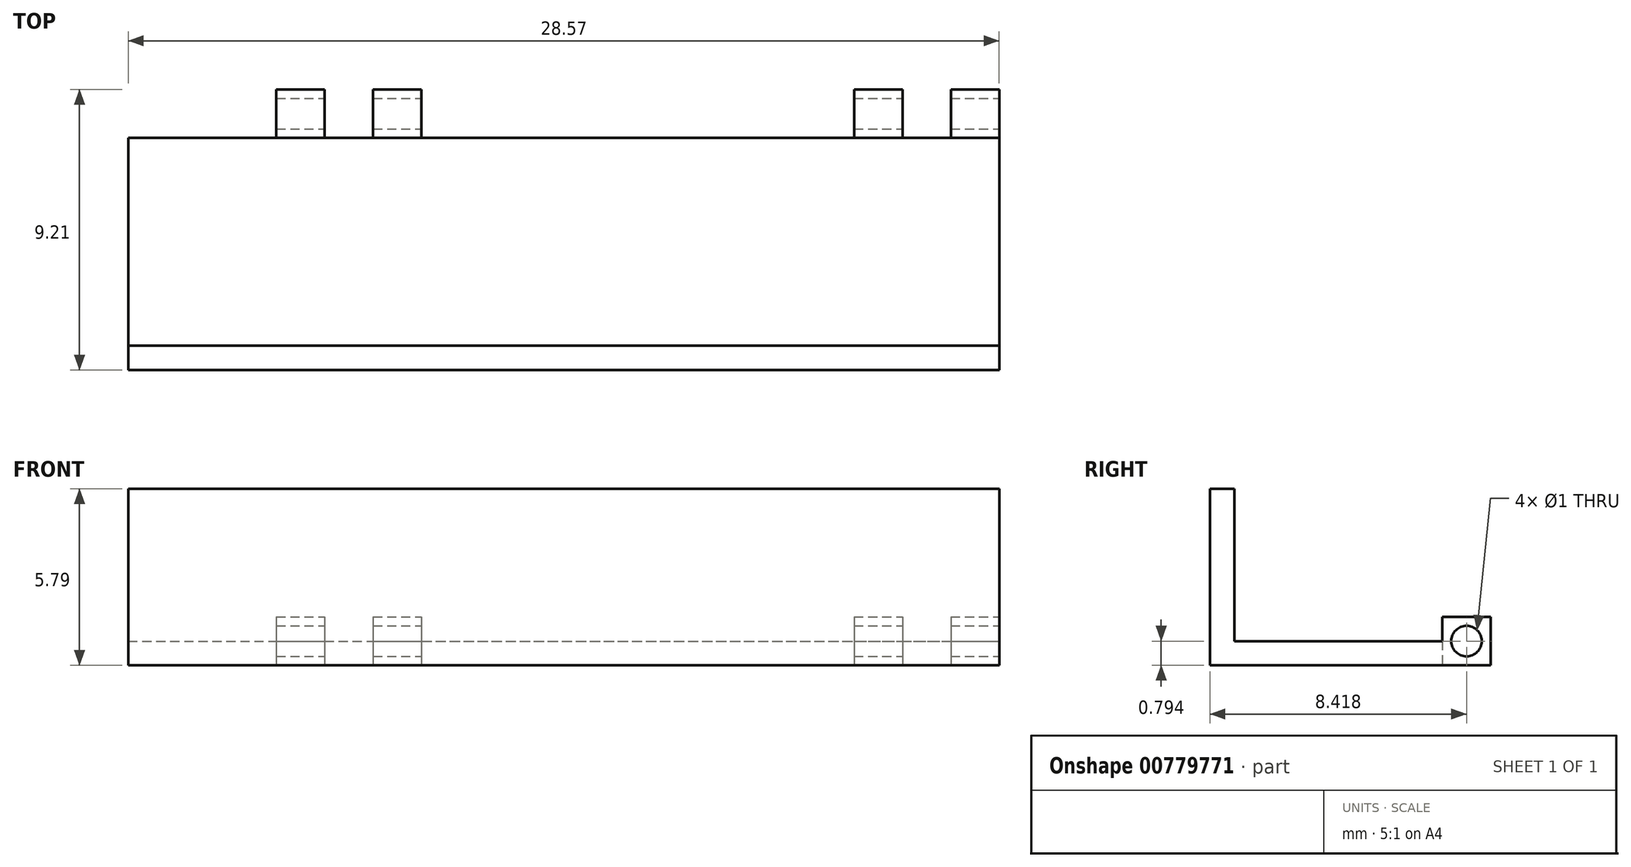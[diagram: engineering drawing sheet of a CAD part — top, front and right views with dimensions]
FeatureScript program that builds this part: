
annotation { "Feature Type Name" : "Feature", "Feature Type Description" : "" }
export const myFeature = defineFeature(function(context is Context, id is Id, definition is map)
    precondition{}
    {
        {
            var Q0;
            Q0=qCreatedBy(makeId("Top.planeOp"),FACE);
            var sketch = newSketch(context, id + "F0", { "sketchPlane" : qUnion([Q0])});
            skLineSegment(sketch, "E0.bottom", {"start": v(-9.35, 12.3) * mm, "end": v(19.22, 12.3) * mm});
            skLineSegment(sketch, "E0.top", {"start": v(-9.35, 4.68) * mm, "end": v(19.22, 4.68) * mm});
            skLineSegment(sketch, "E0.left", {"start": v(-9.35, 12.3) * mm, "end": v(-9.35, 4.68) * mm});
            skLineSegment(sketch, "E0.right", {"start": v(19.22, 12.3) * mm, "end": v(19.22, 4.68) * mm});
            skSolve(sketch);
        }
        {
            var Q0;
            Q0=makeQuery(id+"F0.imprint","IMPRINT",FACE,{"disambiguationData":[TD([[makeQuery(id+"F0.imprint","IMPRINT",EDGE,{"derivedFrom":sQuery(id+"F0.wireOp",EDGE,"E0.bottom")}),-1.0]])]});
            extrude(context, id + "F1", {"entities" : qUnion([Q0]), "depth" : 0.8 * mm, "offsetDistance" : 25.4 * mm});
        }
        {
            var Q0;
            Q0=makeQuery(id+"F1.opExtrude","CAP_FACE",FACE,{"disambiguationData":[OSD([sQuery(id+"F0.wireOp",EDGE,"E0.bottom"),sQuery(id+"F0.wireOp",EDGE,"E0.top"),sQuery(id+"F0.wireOp",EDGE,"E0.left"),sQuery(id+"F0.wireOp",EDGE,"E0.right")])],"isStart":false});
            var sketch = newSketch(context, id + "F2", { "sketchPlane" : qUnion([Q0])});
            skLineSegment(sketch, "E1.bottom", {"start": v(-9.35, 4.68) * mm, "end": v(19.22, 4.68) * mm});
            skLineSegment(sketch, "E1.top", {"start": v(-9.35, 5.48) * mm, "end": v(19.22, 5.48) * mm});
            skLineSegment(sketch, "E1.left", {"start": v(-9.35, 4.68) * mm, "end": v(-9.35, 5.48) * mm});
            skLineSegment(sketch, "E1.right", {"start": v(19.22, 4.68) * mm, "end": v(19.22, 5.48) * mm});
            skSolve(sketch);
        }
        {
            var Q0;
            Q0=makeQuery(id+"F2.imprint","IMPRINT",FACE,{"disambiguationData":[TD([[makeQuery(id+"F2.imprint","IMPRINT",EDGE,{"derivedFrom":sQuery(id+"F2.wireOp",EDGE,"E1.bottom")}),1.0]])]});
            extrude(context, id + "F3", {"entities" : qUnion([Q0]), "operationType" : NewBodyOperationType.ADD, "depth" : 5 * mm, "offsetDistance" : 25.4 * mm});
        }
        {
            var Q0;
            Q0=makeQuery(id+"F1.opExtrude","SWEPT_FACE",FACE,{"disambiguationData":[OSD([sQuery(id+"F0.wireOp",EDGE,"E0.bottom")])]});
            var sketch = newSketch(context, id + "F4", { "sketchPlane" : qUnion([Q0])});
            skLineSegment(sketch, "E2.bottom", {"start": v(-19.22, 0.8) * mm, "end": v(-17.64, 0.8) * mm});
            skLineSegment(sketch, "E2.top", {"start": v(-19.22, 0) * mm, "end": v(-17.64, 0) * mm});
            skLineSegment(sketch, "E2.left", {"start": v(-19.22, 0.8) * mm, "end": v(-19.22, 0) * mm});
            skLineSegment(sketch, "E2.right", {"start": v(-17.64, 0.8) * mm, "end": v(-17.64, 0) * mm});
            skLineSegment(sketch, "E3.bottom", {"start": v(-16.05, 0.8) * mm, "end": v(-14.46, 0.8) * mm});
            skLineSegment(sketch, "E3.top", {"start": v(-16.05, 0) * mm, "end": v(-14.46, 0) * mm});
            skLineSegment(sketch, "E3.left", {"start": v(-16.05, 0.8) * mm, "end": v(-16.05, 0) * mm});
            skLineSegment(sketch, "E3.right", {"start": v(-14.46, 0.8) * mm, "end": v(-14.46, 0) * mm});
            skLineSegment(sketch, "E4.bottom", {"start": v(-0.27, 0.8) * mm, "end": v(1.32, 0.8) * mm});
            skLineSegment(sketch, "E4.top", {"start": v(-0.27, 0) * mm, "end": v(1.32, 0) * mm});
            skLineSegment(sketch, "E4.left", {"start": v(-0.27, 0.8) * mm, "end": v(-0.27, 0) * mm});
            skLineSegment(sketch, "E4.right", {"start": v(1.32, 0.8) * mm, "end": v(1.32, 0) * mm});
            skLineSegment(sketch, "E5.bottom", {"start": v(2.9, 0.8) * mm, "end": v(4.5, 0.8) * mm});
            skLineSegment(sketch, "E5.top", {"start": v(2.9, 0) * mm, "end": v(4.5, 0) * mm});
            skLineSegment(sketch, "E5.left", {"start": v(2.9, 0.8) * mm, "end": v(2.9, 0) * mm});
            skLineSegment(sketch, "E5.right", {"start": v(4.5, 0.8) * mm, "end": v(4.5, 0) * mm});
            skSolve(sketch);
        }
        {
            var Q0;
            Q0=makeQuery(id+"F4.imprint","IMPRINT",FACE,{"disambiguationData":[TD([[makeQuery(id+"F4.imprint","IMPRINT",EDGE,{"derivedFrom":sQuery(id+"F4.wireOp",EDGE,"E2.bottom")}),1.0]])]});
            var Q1;
            Q1=makeQuery(id+"F4.imprint","IMPRINT",FACE,{"disambiguationData":[TD([[makeQuery(id+"F4.imprint","IMPRINT",EDGE,{"derivedFrom":sQuery(id+"F4.wireOp",EDGE,"E3.bottom")}),1.0]])]});
            var Q2;
            Q2=makeQuery(id+"F4.imprint","IMPRINT",FACE,{"disambiguationData":[TD([[makeQuery(id+"F4.imprint","IMPRINT",EDGE,{"derivedFrom":sQuery(id+"F4.wireOp",EDGE,"E4.bottom")}),1.0]])]});
            var Q3;
            Q3=makeQuery(id+"F4.imprint","IMPRINT",FACE,{"disambiguationData":[TD([[makeQuery(id+"F4.imprint","IMPRINT",EDGE,{"derivedFrom":sQuery(id+"F4.wireOp",EDGE,"E5.bottom")}),1.0]])]});
            extrude(context, id + "F5", {"entities" : qUnion([Q0, Q1, Q2, Q3]), "operationType" : NewBodyOperationType.ADD, "depth" : 1.59 * mm, "offsetDistance" : 25.4 * mm});
        }
        {
            var Q0;
            Q0=makeQuery(id+"F5.boolean.opBoolean","MERGE",FACE,{"derivedFrom":[makeQuery(id+"F1.opExtrude","CAP_FACE",FACE,{"disambiguationData":[OSD([sQuery(id+"F0.wireOp",EDGE,"E0.bottom"),sQuery(id+"F0.wireOp",EDGE,"E0.top"),sQuery(id+"F0.wireOp",EDGE,"E0.left"),sQuery(id+"F0.wireOp",EDGE,"E0.right")])],"isStart":false}),makeQuery(id+"F5.opExtrude","SWEPT_FACE",FACE,{"disambiguationData":[OSD([sQuery(id+"F4.wireOp",EDGE,"E2.bottom")])]}),makeQuery(id+"F5.opExtrude","SWEPT_FACE",FACE,{"disambiguationData":[OSD([sQuery(id+"F4.wireOp",EDGE,"E3.bottom")])]}),makeQuery(id+"F5.opExtrude","SWEPT_FACE",FACE,{"disambiguationData":[OSD([sQuery(id+"F4.wireOp",EDGE,"E4.bottom")])]}),makeQuery(id+"F5.opExtrude","SWEPT_FACE",FACE,{"disambiguationData":[OSD([sQuery(id+"F4.wireOp",EDGE,"E5.bottom")])]})]});
            var sketch = newSketch(context, id + "F6", { "sketchPlane" : qUnion([Q0])});
            skLineSegment(sketch, "E6.bottom", {"start": v(-4.5, 13.9) * mm, "end": v(-2.9, 13.9) * mm});
            skLineSegment(sketch, "E6.top", {"start": v(-4.5, 12.3) * mm, "end": v(-2.9, 12.3) * mm});
            skLineSegment(sketch, "E6.left", {"start": v(-4.5, 13.9) * mm, "end": v(-4.5, 12.3) * mm});
            skLineSegment(sketch, "E6.right", {"start": v(-2.9, 13.9) * mm, "end": v(-2.9, 12.3) * mm});
            skLineSegment(sketch, "E7.bottom", {"start": v(-1.32, 13.9) * mm, "end": v(0.27, 13.9) * mm});
            skLineSegment(sketch, "E7.top", {"start": v(-1.32, 12.3) * mm, "end": v(0.27, 12.3) * mm});
            skLineSegment(sketch, "E7.left", {"start": v(-1.32, 13.9) * mm, "end": v(-1.32, 12.3) * mm});
            skLineSegment(sketch, "E7.right", {"start": v(0.27, 13.9) * mm, "end": v(0.27, 12.3) * mm});
            skLineSegment(sketch, "E8.bottom", {"start": v(14.46, 13.9) * mm, "end": v(16.05, 13.9) * mm});
            skLineSegment(sketch, "E8.top", {"start": v(14.46, 12.3) * mm, "end": v(16.05, 12.3) * mm});
            skLineSegment(sketch, "E8.left", {"start": v(14.46, 13.9) * mm, "end": v(14.46, 12.3) * mm});
            skLineSegment(sketch, "E8.right", {"start": v(16.05, 13.9) * mm, "end": v(16.05, 12.3) * mm});
            skLineSegment(sketch, "E9.bottom", {"start": v(17.64, 12.3) * mm, "end": v(19.22, 12.3) * mm});
            skLineSegment(sketch, "E9.top", {"start": v(17.64, 13.9) * mm, "end": v(19.22, 13.9) * mm});
            skLineSegment(sketch, "E9.left", {"start": v(17.64, 12.3) * mm, "end": v(17.64, 13.9) * mm});
            skLineSegment(sketch, "E9.right", {"start": v(19.22, 12.3) * mm, "end": v(19.22, 13.9) * mm});
            skSolve(sketch);
        }
        {
            var Q0;
            Q0 = qSketchRegion(id + "F6", true);
            extrude(context, id + "F7", {"entities" : qUnion([Q0]), "operationType" : NewBodyOperationType.ADD, "depth" : 0.8 * mm, "offsetDistance" : 25.4 * mm});
        }
        {
            var Q0;
            Q0=makeQuery(id+"F7.boolean.opBoolean","MERGE",FACE,{"derivedFrom":[makeQuery(id+"F5.boolean.opBoolean","MERGE",FACE,{"derivedFrom":[makeQuery(id+"F3.boolean.opBoolean","MERGE",FACE,{"derivedFrom":[makeQuery(id+"F1.opExtrude","SWEPT_FACE",FACE,{"disambiguationData":[OSD([sQuery(id+"F0.wireOp",EDGE,"E0.right")])]}),makeQuery(id+"F3.opExtrude","SWEPT_FACE",FACE,{"disambiguationData":[OSD([sQuery(id+"F2.wireOp",EDGE,"E1.right")])]})]}),makeQuery(id+"F5.opExtrude","SWEPT_FACE",FACE,{"disambiguationData":[OSD([sQuery(id+"F4.wireOp",EDGE,"E2.left")])]})]}),makeQuery(id+"F7.opExtrude","SWEPT_FACE",FACE,{"disambiguationData":[OSD([sQuery(id+"F6.wireOp",EDGE,"E9.right")])]})]});
            var sketch = newSketch(context, id + "F8", { "sketchPlane" : qUnion([Q0])});
            skCircle(sketch, "E10", {"center": v(13.1, 0.8) * mm, "radius": 0.5 * mm});
            skPoint(sketch, "E10.centerSnap0", {"position": v(13.9, 0.8) * mm});
            skPoint(sketch, "E10.centerSnap1", {"position": v(13.1, 1.59) * mm});
            skSolve(sketch);
        }
        {
            var Q0;
            Q0=makeQuery(id+"F8.imprint","IMPRINT",FACE,{"disambiguationData":[TD([[makeQuery(id+"F8.imprint","IMPRINT",EDGE,{"derivedFrom":sQuery(id+"F8.wireOp",EDGE,"E10")}),1.0]])]});
            extrude(context, id + "F9", {"entities" : qUnion([Q0]), "operationType" : NewBodyOperationType.REMOVE, "oppositeDirection" : true, "depth" : 25.4 * mm, "offsetDistance" : 25.4 * mm});
        }
    });
